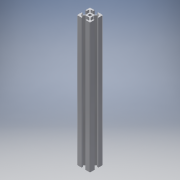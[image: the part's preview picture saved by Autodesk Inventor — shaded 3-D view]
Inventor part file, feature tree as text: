
AUTODESK INVENTOR PART (.ipt)
format: ipt  version: 2016 (Build 200138000, 138)  size: 222,720 bytes
history: native  units: mm
features: other x7, sketch x2, extrude x1, hole x1
ambient origin geometry x8: Origin, YZ Plane, XZ Plane, XY Plane, X Axis, Y Axis, Z Axis, Center Point
bodies: Solid1 (feature_tree)
feature tree (11):
  extrude  "Extrusion1"  TaperAngle=0.0deg  [1 undecoded]
  hole  "Hole1"  [1 undecoded]
  other  "C1_XY"
  other  "C1_YZ"
  other  "C1_ZX"
  other  "C1_X"
  other  "C1_Y"
  other  "C1_Z"
  other  "C1_Center"
  sketch  "Sketch_75"  dims[d2=4.2mm d3=6.0mm d4=4.0mm d5=2.0mm d6=90.0deg d7=200.0mm d8=0.0mm d9=0.0mm]
  sketch  "Sketch2"  dims[d0=200.0mm d1=0.0mm]
note: 2 required parameter values undecoded (feature->parameter linkage not recoverable at this tier; creation-order binding heuristic only, values carry confidence <= 0.55)
